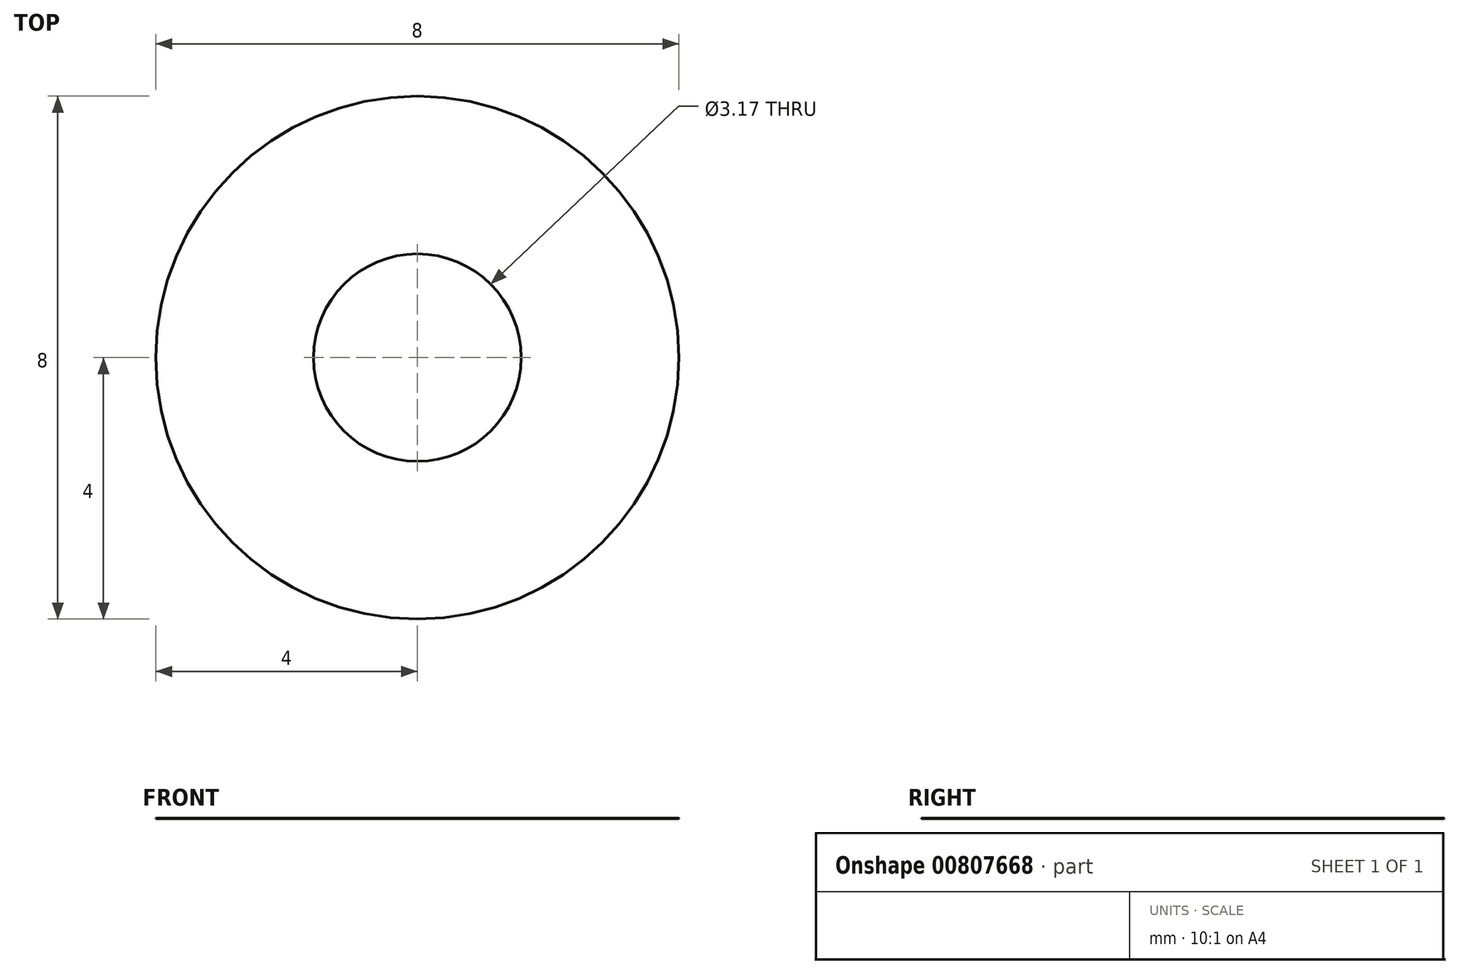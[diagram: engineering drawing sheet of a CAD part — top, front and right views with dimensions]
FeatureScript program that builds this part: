
annotation { "Feature Type Name" : "Feature", "Feature Type Description" : "" }
export const myFeature = defineFeature(function(context is Context, id is Id, definition is map)
    precondition{}
    {
        {
            var Q0;
            Q0=qCreatedBy(makeId("Top.planeOp"),FACE);
            var sketch = newSketch(context, id + "F0", { "sketchPlane" : qUnion([Q0])});
            skCircle(sketch, "E0", {"center": v(0, 0) * mm, "radius": 4 * mm});
            skCircle(sketch, "E1", {"center": v(0, 0) * mm, "radius": 1.59 * mm});
            skSolve(sketch);
        }
        {
            var Q0;
            Q0=makeQuery(id+"F0.imprint","IMPRINT",FACE,{"disambiguationData":[TD([[makeQuery(id+"F0.imprint","IMPRINT",EDGE,{"derivedFrom":sQuery(id+"F0.wireOp",EDGE,"E0")}),1.0]])]});
            extrude(context, id + "F1", {"entities" : qUnion([Q0]), "depth" : 1 / 203.2 * mm, "offsetDistance" : 25.4 * mm});
        }
    });
